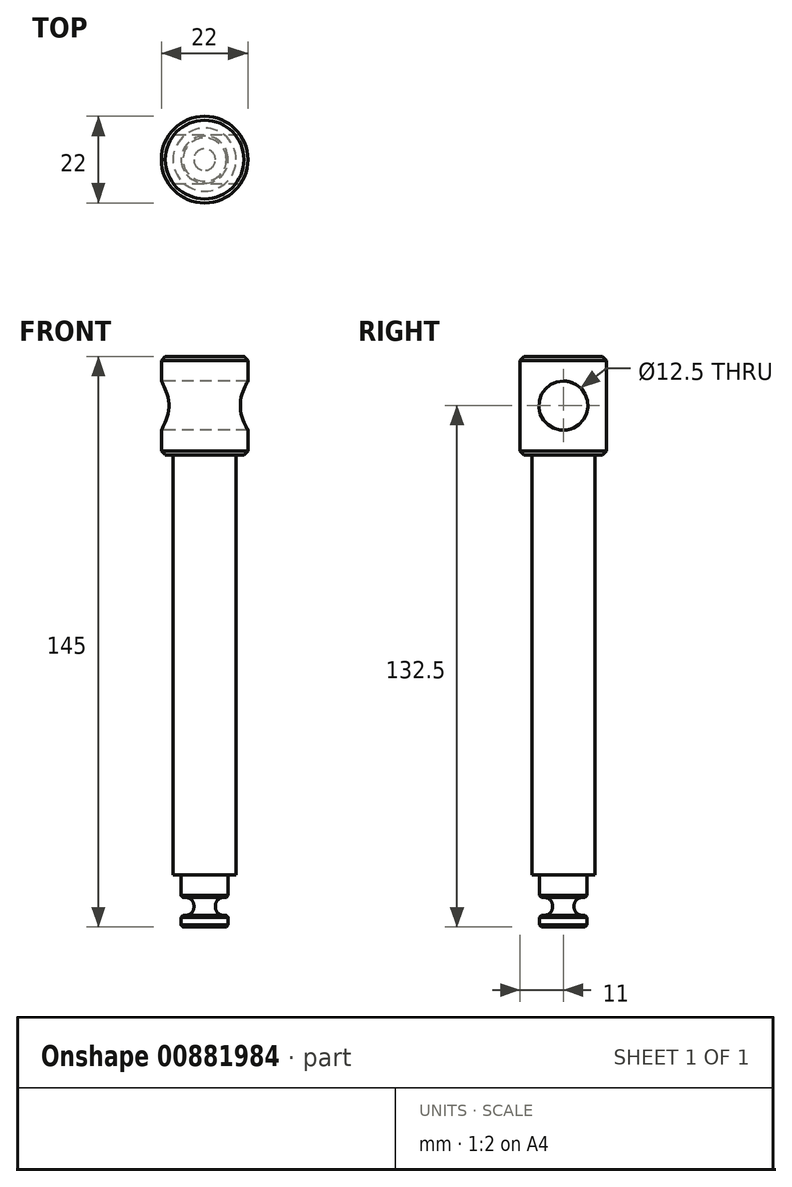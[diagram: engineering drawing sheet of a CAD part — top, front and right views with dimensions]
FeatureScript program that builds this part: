
annotation { "Feature Type Name" : "Feature", "Feature Type Description" : "" }
export const myFeature = defineFeature(function(context is Context, id is Id, definition is map)
    precondition{}
    {
        {
            var Q0;
            Q0=qCreatedBy(makeId("Front.planeOp"),FACE);
            var sketch = newSketch(context, id + "F0", { "sketchPlane" : qUnion([Q0])});
            skLineSegment(sketch, "E0", {"start": v(0, 0) * mm, "end": v(0, 99.13) * mm, "construction": true});
            skLineSegment(sketch, "E1", {"start": v(0, 0) * mm, "end": v(-6, 0) * mm});
            skLineSegment(sketch, "E2", {"start": v(-6, 0) * mm, "end": v(-6, 3) * mm});
            skLineSegment(sketch, "E3", {"start": v(-6, 3) * mm, "end": v(-2.75, 3) * mm});
            skLineSegment(sketch, "E4", {"start": v(-2.75, 3) * mm, "end": v(-2.75, 7.5) * mm});
            skLineSegment(sketch, "E5", {"start": v(-2.75, 7.5) * mm, "end": v(-6, 7.5) * mm});
            skLineSegment(sketch, "E6", {"start": v(-6, 7.5) * mm, "end": v(-6, 13.25) * mm});
            skLineSegment(sketch, "E7", {"start": v(-6, 13.25) * mm, "end": v(-8, 13.25) * mm});
            skLineSegment(sketch, "E8", {"start": v(-8, 13.25) * mm, "end": v(-8, 120) * mm});
            skLineSegment(sketch, "E9", {"start": v(-8, 120) * mm, "end": v(-11, 120) * mm});
            skLineSegment(sketch, "E10", {"start": v(-11, 120) * mm, "end": v(-11, 145) * mm});
            skLineSegment(sketch, "E11", {"start": v(-11, 145) * mm, "end": v(0, 145) * mm});
            skLineSegment(sketch, "E12", {"start": v(0, 145) * mm, "end": v(0, 0) * mm});
            skSolve(sketch);
        }
        {
            var Q0;
            Q0 = qSketchRegion(id + "F0", true);
            var Q1;
            Q1=sQuery(id+"F0.wireOp",EDGE,"E0");
            revolve(context, id + "F1", {"surfaceOperationType" : NewSurfaceOperationType.NEW, "entities" : qUnion([Q0]), "axis" : qUnion([Q1]), "revolveType" : RevolveType.FULL});
        }
        {
            var Q0;
            Q0=makeQuery(id+"F1.opRevolve","SWEPT_FACE",FACE,{"disambiguationData":[OSD([sQuery(id+"F0.wireOp",EDGE,"E4")])]});
            fillet(context, id + "F2", {"entities" : qUnion([Q0]), "radius" : 2 * mm, "tangentPropagation" : true, "allowEdgeOverflow" : false});
        }
        {
            var Q0;
            Q0=makeQuery(id+"F1.opRevolve","SWEPT_EDGE",EDGE,{"disambiguationData":[OSD([sQuery(id+"F0.wireOp",EDGE,"E5"),sQuery(id+"F0.wireOp",EDGE,"E6")])]});
            var Q1;
            Q1=makeQuery(id+"F1.opRevolve","SWEPT_EDGE",EDGE,{"disambiguationData":[OSD([sQuery(id+"F0.wireOp",EDGE,"E2"),sQuery(id+"F0.wireOp",EDGE,"E3")])]});
            var Q2;
            Q2=makeQuery(id+"F1.opRevolve","SWEPT_EDGE",EDGE,{"disambiguationData":[OSD([sQuery(id+"F0.wireOp",EDGE,"E1"),sQuery(id+"F0.wireOp",EDGE,"E2")])]});
            chamfer(context, id + "F3", {"entities" : qUnion([Q0, Q1, Q2]), "width" : 0.5 * mm, "tangentPropagation" : true});
        }
        {
            var Q0;
            Q0=qCreatedBy(makeId("Right.planeOp"),FACE);
            var sketch = newSketch(context, id + "F4", { "sketchPlane" : qUnion([Q0])});
            skCircle(sketch, "E13", {"center": v(0, 132.5) * mm, "radius": 6.25 * mm});
            skLineSegment(sketch, "E14", {"start": v(0, 132.5) * mm, "end": v(0, 0) * mm, "construction": true});
            skSolve(sketch);
        }
        {
            var Q0;
            Q0 = qSketchRegion(id + "F4", true);
            extrude(context, id + "F5", {"entities" : qUnion([Q0]), "operationType" : NewBodyOperationType.REMOVE, "depth" : 40.2 * mm, "offsetDistance" : 25 * mm, "symmetric" : true});
        }
        {
            var Q0;
            Q0=makeQuery(id+"F1.opRevolve","SWEPT_EDGE",EDGE,{"disambiguationData":[OSD([sQuery(id+"F0.wireOp",EDGE,"E10"),sQuery(id+"F0.wireOp",EDGE,"E11")])]});
            var Q1;
            Q1=makeQuery(id+"F1.opRevolve","SWEPT_EDGE",EDGE,{"disambiguationData":[OSD([sQuery(id+"F0.wireOp",EDGE,"E9"),sQuery(id+"F0.wireOp",EDGE,"E10")])]});
            chamfer(context, id + "F6", {"entities" : qUnion([Q0, Q1]), "width" : 1 * mm, "tangentPropagation" : true});
        }
    });
